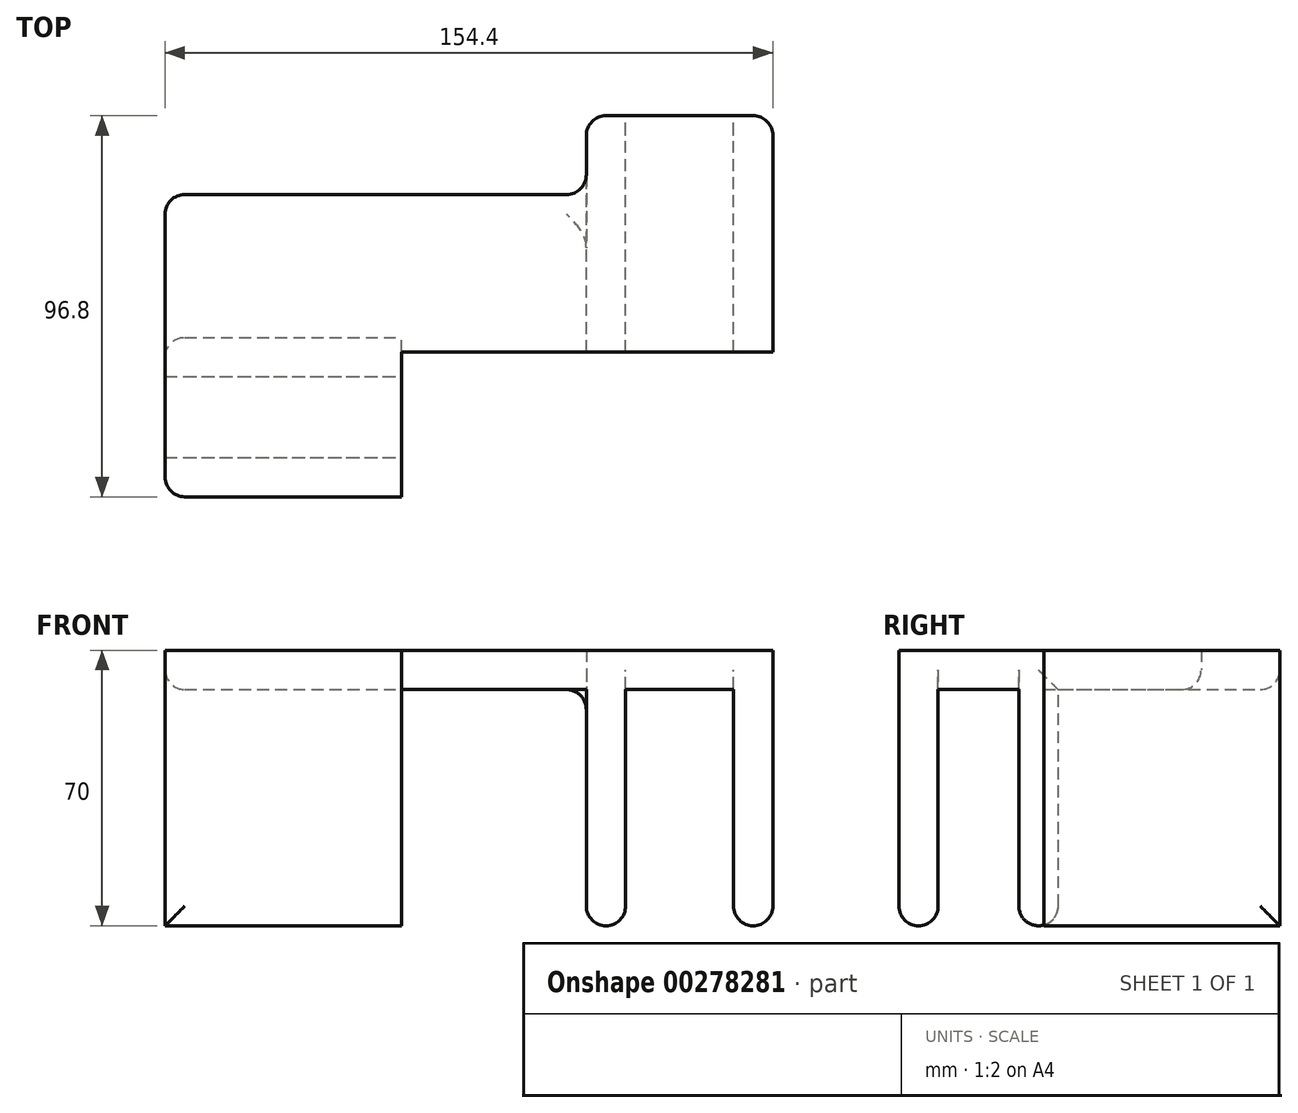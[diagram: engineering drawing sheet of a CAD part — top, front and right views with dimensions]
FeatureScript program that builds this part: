
annotation { "Feature Type Name" : "Feature", "Feature Type Description" : "" }
export const myFeature = defineFeature(function(context is Context, id is Id, definition is map)
    precondition{}
    {
        {
            var Q0;
            Q0=qCreatedBy(makeId("Top.planeOp"),FACE);
            var sketch = newSketch(context, id + "F0", { "sketchPlane" : qUnion([Q0])});
            skLineSegment(sketch, "E0", {"start": v(0, 0) * mm, "end": v(50, 0) * mm, "construction": true});
            skLineSegment(sketch, "E1", {"start": v(0, 18.5) * mm, "end": v(50, 18.5) * mm, "construction": true});
            skLineSegment(sketch, "E2.bottom", {"start": v(50, 24.8) * mm, "end": v(138.7, 24.8) * mm, "construction": true});
            skLineSegment(sketch, "E2.top", {"start": v(50, -6.3) * mm, "end": v(138.7, -6.3) * mm, "construction": true});
            skLineSegment(sketch, "E2.left", {"start": v(50, 24.8) * mm, "end": v(50, -6.3) * mm, "construction": true});
            skLineSegment(sketch, "E2.right", {"start": v(138.7, 24.8) * mm, "end": v(138.7, -6.3) * mm, "construction": true});
            skLineSegment(sketch, "E3", {"start": v(107, 24.8) * mm, "end": v(107, 74.8) * mm, "construction": true});
            skLineSegment(sketch, "E4", {"start": v(132.4, 24.8) * mm, "end": v(132.4, 74.8) * mm, "construction": true});
            skLineSegment(sketch, "E5", {"start": v(132.4, 74.8) * mm, "end": v(107, 74.8) * mm, "construction": true});
            skLineSegment(sketch, "E6", {"start": v(0, 18.5) * mm, "end": v(0, 0) * mm, "construction": true});
            skSolve(sketch);
        }
        {
            var Q0;
            Q0=qCreatedBy(makeId("Top.planeOp"),FACE);
            var sketch = newSketch(context, id + "F1", { "sketchPlane" : qUnion([Q0])});
            skLineSegment(sketch, "E7", {"start": v(-11, -11) * mm, "end": v(-11, 65.8) * mm});
            skLineSegment(sketch, "E8", {"start": v(96, 85.8) * mm, "end": v(143.4, 85.8) * mm});
            skLineSegment(sketch, "E9", {"start": v(143.4, 85.8) * mm, "end": v(143.4, 25.8) * mm});
            skLineSegment(sketch, "E10", {"start": v(143.4, 25.8) * mm, "end": v(49, 25.8) * mm});
            skLineSegment(sketch, "E11", {"start": v(49, 25.8) * mm, "end": v(49, -11) * mm});
            skLineSegment(sketch, "E12", {"start": v(49, -11) * mm, "end": v(-11, -11) * mm});
            skLineSegment(sketch, "E13", {"start": v(-11, -1) * mm, "end": v(49, -1) * mm, "construction": true});
            skLineSegment(sketch, "E14", {"start": v(-11, 19.5) * mm, "end": v(49, 19.5) * mm, "construction": true});
            skLineSegment(sketch, "E15", {"start": v(106, 85.8) * mm, "end": v(106, 25.8) * mm, "construction": true});
            skLineSegment(sketch, "E16", {"start": v(133.4, 85.8) * mm, "end": v(133.4, 25.8) * mm, "construction": true});
            skLineSegment(sketch, "E17", {"start": v(-11, 65.8) * mm, "end": v(96, 65.8) * mm});
            skLineSegment(sketch, "E18", {"start": v(96, 65.8) * mm, "end": v(96, 85.8) * mm});
            skSolve(sketch);
        }
        {
            var Q0;
            Q0 = qSketchRegion(id + "F1", true);
            extrude(context, id + "F2", {"entities" : qUnion([Q0]), "depth" : 10 * mm, "offsetDistance" : 25 * mm});
        }
        {
            var Q0;
            Q0=makeQuery(id+"F2.opExtrude","CAP_FACE",FACE,{"disambiguationData":[OSD([sQuery(id+"F1.wireOp",EDGE,"E7"),sQuery(id+"F1.wireOp",EDGE,"E8"),sQuery(id+"F1.wireOp",EDGE,"E9"),sQuery(id+"F1.wireOp",EDGE,"E10"),sQuery(id+"F1.wireOp",EDGE,"E11"),sQuery(id+"F1.wireOp",EDGE,"E12")])],"isStart":true});
            var sketch = newSketch(context, id + "F3", { "sketchPlane" : qUnion([Q0])});
            skLineSegment(sketch, "E19.bottom", {"start": v(-11, 11) * mm, "end": v(49, 11) * mm});
            skLineSegment(sketch, "E19.top", {"start": v(-11, 1) * mm, "end": v(49, 1) * mm});
            skLineSegment(sketch, "E19.left", {"start": v(-11, 11) * mm, "end": v(-11, 1) * mm});
            skLineSegment(sketch, "E19.right", {"start": v(49, 11) * mm, "end": v(49, 1) * mm});
            skLineSegment(sketch, "E20.bottom", {"start": v(-11, -19.5) * mm, "end": v(49, -19.5) * mm});
            skLineSegment(sketch, "E20.top", {"start": v(-11, -29.5) * mm, "end": v(49, -29.5) * mm});
            skLineSegment(sketch, "E20.left", {"start": v(-11, -19.5) * mm, "end": v(-11, -29.5) * mm});
            skLineSegment(sketch, "E20.right", {"start": v(49, -19.5) * mm, "end": v(49, -29.5) * mm});
            skLineSegment(sketch, "E21.bottom", {"start": v(96, -25.8) * mm, "end": v(106, -25.8) * mm});
            skLineSegment(sketch, "E21.top", {"start": v(96, -85.8) * mm, "end": v(106, -85.8) * mm});
            skLineSegment(sketch, "E21.left", {"start": v(96, -25.8) * mm, "end": v(96, -85.8) * mm});
            skLineSegment(sketch, "E21.right", {"start": v(106, -25.8) * mm, "end": v(106, -85.8) * mm});
            skLineSegment(sketch, "E22.bottom", {"start": v(143.4, -25.8) * mm, "end": v(133.4, -25.8) * mm});
            skLineSegment(sketch, "E22.top", {"start": v(143.4, -85.8) * mm, "end": v(133.4, -85.8) * mm});
            skLineSegment(sketch, "E22.left", {"start": v(143.4, -25.8) * mm, "end": v(143.4, -85.8) * mm});
            skLineSegment(sketch, "E22.right", {"start": v(133.4, -25.8) * mm, "end": v(133.4, -85.8) * mm});
            skSolve(sketch);
        }
        {
            var Q0;
            Q0 = qSketchRegion(id + "F3", true);
            extrude(context, id + "F4", {"entities" : qUnion([Q0]), "operationType" : NewBodyOperationType.ADD, "depth" : 60 * mm, "offsetDistance" : 25 * mm});
        }
        {
            var Q0;
            Q0=makeQuery(id+"F2.opExtrude","SWEPT_EDGE",EDGE,{"disambiguationData":[OSD([sQuery(id+"F1.wireOp",EDGE,"E17"),sQuery(id+"F1.wireOp",EDGE,"E18")])]});
            var Q1;
            Q1=makeQuery(id+"F4.boolean.opBoolean","MERGE",EDGE,{"derivedFrom":[makeQuery(id+"F2.opExtrude","SWEPT_EDGE",EDGE,{"disambiguationData":[OSD([sQuery(id+"F1.wireOp",EDGE,"E8"),sQuery(id+"F1.wireOp",EDGE,"E18")])]}),makeQuery(id+"F4.opExtrude","SWEPT_EDGE",EDGE,{"disambiguationData":[OSD([sQuery(id+"F3.wireOp",EDGE,"E21.top"),sQuery(id+"F3.wireOp",EDGE,"E21.left")])]})]});
            var Q2;
            Q2=makeQuery(id+"F4.boolean.opBoolean","MERGE",EDGE,{"derivedFrom":[makeQuery(id+"F2.opExtrude","SWEPT_EDGE",EDGE,{"disambiguationData":[OSD([sQuery(id+"F1.wireOp",EDGE,"E8"),sQuery(id+"F1.wireOp",EDGE,"E9")])]}),makeQuery(id+"F4.opExtrude","SWEPT_EDGE",EDGE,{"disambiguationData":[OSD([sQuery(id+"F3.wireOp",EDGE,"E22.top"),sQuery(id+"F3.wireOp",EDGE,"E22.left")])]})]});
            var Q3;
            Q3=makeQuery(id+"F2.opExtrude","SWEPT_EDGE",EDGE,{"disambiguationData":[OSD([sQuery(id+"F1.wireOp",EDGE,"E7"),sQuery(id+"F1.wireOp",EDGE,"E17")])]});
            var Q4;
            Q4=makeQuery(id+"F4.opExtrude","SWEPT_EDGE",EDGE,{"disambiguationData":[OSD([sQuery(id+"F1.wireOp",EDGE,"E7"),sQuery(id+"F3.wireOp",EDGE,"E20.top"),sQuery(id+"F3.wireOp",EDGE,"E20.left")])]});
            var Q5;
            Q5=makeQuery(id+"F4.boolean.opBoolean","MERGE",EDGE,{"derivedFrom":[makeQuery(id+"F2.opExtrude","SWEPT_EDGE",EDGE,{"disambiguationData":[OSD([sQuery(id+"F1.wireOp",EDGE,"E7"),sQuery(id+"F1.wireOp",EDGE,"E12")])]}),makeQuery(id+"F4.opExtrude","SWEPT_EDGE",EDGE,{"disambiguationData":[OSD([sQuery(id+"F3.wireOp",EDGE,"E19.bottom"),sQuery(id+"F3.wireOp",EDGE,"E19.left")])]})]});
            var Q6;
            Q6=makeQuery(id+"F2.opExtrude","CAP_EDGE",EDGE,{"disambiguationData":[OSD([sQuery(id+"F1.wireOp",EDGE,"E8")])],"isStart":true});
            var Q7;
            Q7=makeQuery(id+"F2.opExtrude","CAP_EDGE",EDGE,{"disambiguationData":[OSD([sQuery(id+"F1.wireOp",EDGE,"E17")])],"isStart":true});
            var Q8;
            {var subQ0=sQuery(id+"F1.wireOp",EDGE,"E17");var subQ1=sQuery(id+"F1.wireOp",EDGE,"E7");Q8=makeQuery(id+"F4.boolean.opBoolean","SPLIT",EDGE,{"disambiguationData":[TD([makeQuery(id+"F2.opExtrude","SWEPT_FACE",FACE,{"disambiguationData":[OSD([subQ0])]})])],"derivedFrom":makeQuery(id+"F2.opExtrude","CAP_EDGE",EDGE,{"disambiguationData":[OSD([subQ1])],"isStart":true})});}
            var Q9;
            {var subQ0=sQuery(id+"F1.wireOp",EDGE,"E7");Q9=makeQuery(id+"F4.boolean.opBoolean","SPLIT",EDGE,{"disambiguationData":[TD([makeQuery(id+"F4.opExtrude","SWEPT_FACE",FACE,{"disambiguationData":[OSD([sQuery(id+"F3.wireOp",EDGE,"E19.top")])]})])],"derivedFrom":makeQuery(id+"F2.opExtrude","CAP_EDGE",EDGE,{"disambiguationData":[OSD([subQ0])],"isStart":true})});}
            var Q10;
            Q10=makeQuery(id+"F4.opExtrude","CAP_EDGE",EDGE,{"disambiguationData":[OSD([sQuery(id+"F3.wireOp",EDGE,"E22.right")])],"isStart":false});
            var Q11;
            Q11=makeQuery(id+"F4.opExtrude","CAP_EDGE",EDGE,{"disambiguationData":[OSD([sQuery(id+"F3.wireOp",EDGE,"E21.right")])],"isStart":false});
            var Q12;
            Q12=makeQuery(id+"F4.opExtrude","CAP_EDGE",EDGE,{"disambiguationData":[OSD([sQuery(id+"F3.wireOp",EDGE,"E21.left")])],"isStart":false});
            var Q13;
            Q13=makeQuery(id+"F4.opExtrude","CAP_EDGE",EDGE,{"disambiguationData":[OSD([sQuery(id+"F3.wireOp",EDGE,"E22.left")])],"isStart":false});
            var Q14;
            Q14=makeQuery(id+"F4.opExtrude","CAP_EDGE",EDGE,{"disambiguationData":[OSD([sQuery(id+"F3.wireOp",EDGE,"E20.top")])],"isStart":true});
            var Q15;
            Q15=makeQuery(id+"F4.opExtrude","CAP_EDGE",EDGE,{"disambiguationData":[OSD([sQuery(id+"F3.wireOp",EDGE,"E20.top")])],"isStart":false});
            var Q16;
            Q16=makeQuery(id+"F4.opExtrude","CAP_EDGE",EDGE,{"disambiguationData":[OSD([sQuery(id+"F3.wireOp",EDGE,"E19.bottom")])],"isStart":false});
            var Q17;
            Q17=makeQuery(id+"F4.opExtrude","CAP_EDGE",EDGE,{"disambiguationData":[OSD([sQuery(id+"F3.wireOp",EDGE,"E19.top")])],"isStart":false});
            var Q18;
            Q18=makeQuery(id+"F4.opExtrude","CAP_EDGE",EDGE,{"disambiguationData":[OSD([sQuery(id+"F3.wireOp",EDGE,"E20.bottom")])],"isStart":false});
            fillet(context, id + "F5", {"entities" : qUnion([Q0, Q1, Q2, Q3, Q4, Q5, Q6, Q7, Q8, Q9, Q10, Q11, Q12, Q13, Q14, Q15, Q16, Q17, Q18]), "radius" : 5 * mm, "tangentPropagation" : true, "defaultsChanged" : false, "vertexSettings" : [], "allowEdgeOverflow" : false});
        }
    });
